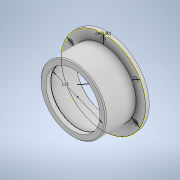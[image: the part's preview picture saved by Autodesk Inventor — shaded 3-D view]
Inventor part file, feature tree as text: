
AUTODESK INVENTOR PART (.ipt)
format: ipt  version: 2021.2 (Build 252289000, 289)  size: 181,760 bytes
history: native  units: mm
features: sketch x12, extrude x3, chamfer x2, hole x2, other x1, fillet x1
ambient origin geometry x8: Origin, YZ Plane, XZ Plane, XY Plane, X Axis, Y Axis, Z Axis, Center Point
bodies: Body1 (feature_tree)
feature tree (21):
  other  "Твердое тело1"
  extrude  "Выдавливание1"  Depth=180.0mm
  sketch  "Эскиз2"
  extrude  "Выдавливание2"  Depth=8.0mm TaperAngle=0.0deg
  extrude  "Выдавливание3"  Depth=140.0mm
  chamfer  "Фаска1"  Distance=65.0mm
  chamfer  "Фаска2"  Distance=130.0mm
  sketch  "Эскиз5"
  sketch  "Эскиз6"
  sketch  "Эскиз7"
  sketch  "Эскиз8"
  sketch  "Эскиз9"
  sketch  "Эскиз10"
  sketch  "Эскиз11"
  hole  "Отверстие1"  [1 undecoded]
  hole  "Отверстие2"  [1 undecoded]
  fillet  "Сопряжение1"  Radius=2.0mm
  sketch  "Эскиз1"
  sketch  "Эскиз3"
  sketch  "Эскиз4"
  sketch  "Эскиз12"
note: 2 required parameter values undecoded (feature->parameter linkage not recoverable at this tier; creation-order binding heuristic only, values carry confidence <= 0.55)
